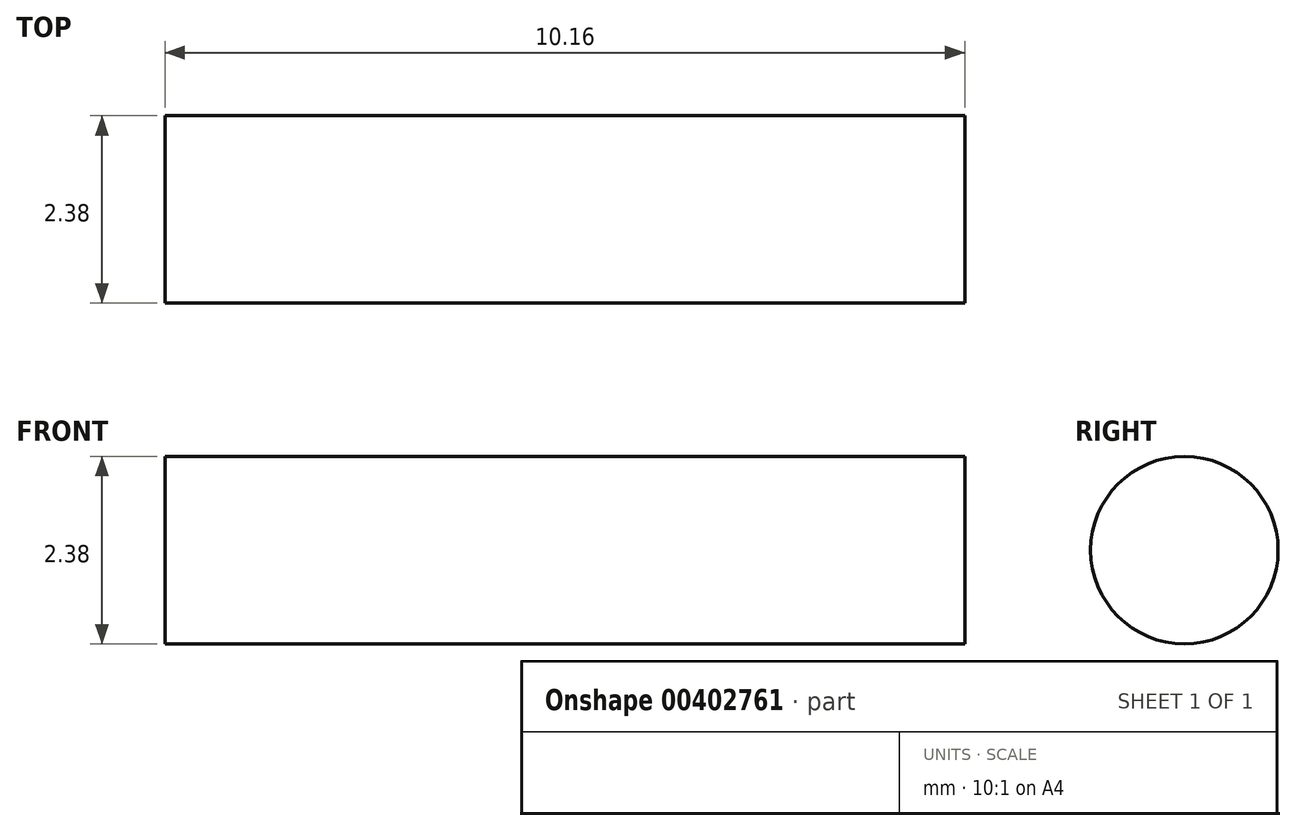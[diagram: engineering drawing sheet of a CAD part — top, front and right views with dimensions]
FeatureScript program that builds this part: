
annotation { "Feature Type Name" : "Feature", "Feature Type Description" : "" }
export const myFeature = defineFeature(function(context is Context, id is Id, definition is map)
    precondition{}
    {
        {
            var Q0;
            Q0=qCreatedBy(makeId("Right.planeOp"),FACE);
            var sketch = newSketch(context, id + "F0", { "sketchPlane" : qUnion([Q0])});
            skCircle(sketch, "E0", {"center": v(0, 0) * mm, "radius": 1.2 * mm});
            skSolve(sketch);
        }
        {
            var Q0;
            Q0 = qSketchRegion(id + "F0", true);
            extrude(context, id + "F1", {"entities" : qUnion([Q0]), "endBound" : BoundingType.SYMMETRIC, "depth" : 10.16 * mm});
        }
    });
